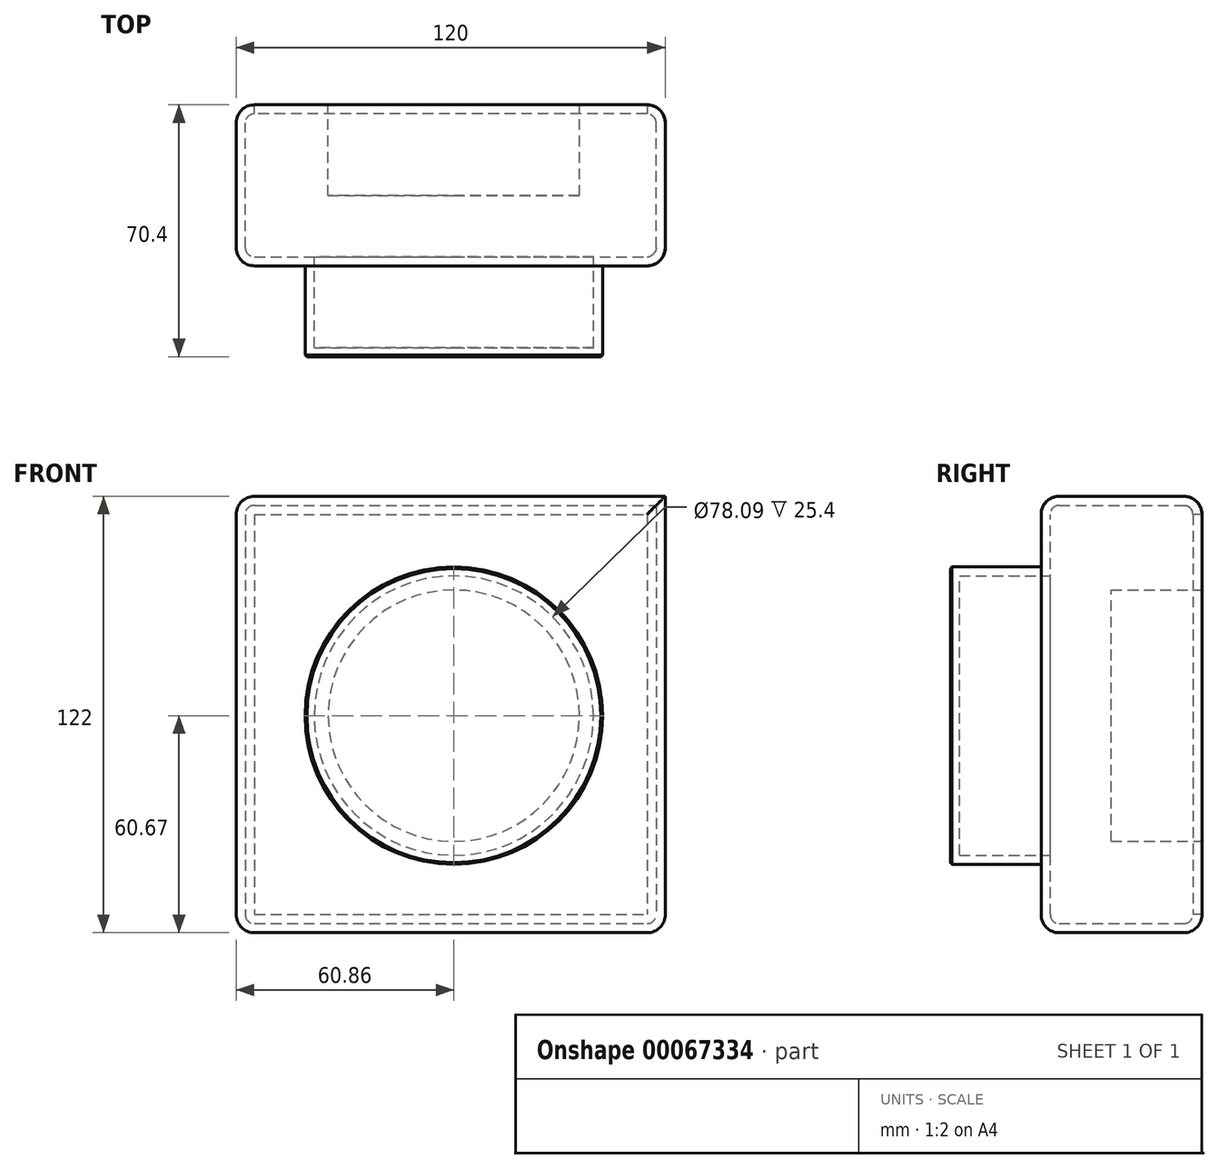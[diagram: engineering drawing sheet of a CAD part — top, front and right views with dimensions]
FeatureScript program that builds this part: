
annotation { "Feature Type Name" : "Feature", "Feature Type Description" : "" }
export const myFeature = defineFeature(function(context is Context, id is Id, definition is map)
    precondition{}
    {
        {
            var Q0;
            Q0=qCreatedBy(makeId("Front.planeOp"),FACE);
            var sketch = newSketch(context, id + "F0", { "sketchPlane" : qUnion([Q0])});
            skLineSegment(sketch, "E0.bottom", {"start": v(-60.86, 61.33) * mm, "end": v(59.14, 61.33) * mm});
            skLineSegment(sketch, "E0.top", {"start": v(-60.86, -60.67) * mm, "end": v(59.14, -60.67) * mm});
            skLineSegment(sketch, "E0.left", {"start": v(-60.86, 61.33) * mm, "end": v(-60.86, -60.67) * mm});
            skLineSegment(sketch, "E0.right", {"start": v(59.14, 61.33) * mm, "end": v(59.14, -60.67) * mm});
            skSolve(sketch);
        }
        {
            var Q0;
            Q0=makeQuery(id+"F0.imprint","IMPRINT",FACE,{"disambiguationData":[TD([[makeQuery(id+"F0.imprint","IMPRINT",EDGE,{"derivedFrom":sQuery(id+"F0.wireOp",EDGE,"E0.bottom")}),-1.0]])]});
            extrude(context, id + "F1", {"entities" : qUnion([Q0]), "depth" : 45 * mm});
        }
        {
            var Q0;
            Q0=makeQuery(id+"F1.opExtrude","CAP_FACE",FACE,{"disambiguationData":[OSD([sQuery(id+"F0.wireOp",EDGE,"E0.bottom"),sQuery(id+"F0.wireOp",EDGE,"E0.top"),sQuery(id+"F0.wireOp",EDGE,"E0.left"),sQuery(id+"F0.wireOp",EDGE,"E0.right")])],"isStart":false});
            var sketch = newSketch(context, id + "F2", { "sketchPlane" : qUnion([Q0])});
            skCircle(sketch, "E1", {"center": v(0, 0) * mm, "radius": 41.58 * mm});
            skSolve(sketch);
        }
        {
            var Q0;
            Q0=makeQuery(id+"F2.imprint","IMPRINT",FACE,{"disambiguationData":[TD([[makeQuery(id+"F2.imprint","IMPRINT",EDGE,{"derivedFrom":sQuery(id+"F2.wireOp",EDGE,"E1")}),1.0]])]});
            var sketch = newSketch(context, id + "F3", { "sketchPlane" : qUnion([Q0])});
            skCircle(sketch, "E2", {"center": v(0, 0) * mm, "radius": 35.37 * mm});
            skSolve(sketch);
        }
        {
            var Q0;
            Q0 = qSketchRegion(id + "F3", true);
            var Q1;
            Q1 = qSketchRegion(id + "F2", true);
            extrude(context, id + "F4", {"entities" : qUnion([Q0, Q1]), "operationType" : NewBodyOperationType.REMOVE, "depth" : 50.8 * mm});
        }
        {
            var Q0;
            Q0=makeQuery(id+"F1.opExtrude","SWEPT_EDGE",EDGE,{"disambiguationData":[OSD([sQuery(id+"F0.wireOp",EDGE,"E0.bottom"),sQuery(id+"F0.wireOp",EDGE,"E0.left")])]});
            var Q1;
            Q1=makeQuery(id+"F1.opExtrude","SWEPT_FACE",FACE,{"disambiguationData":[OSD([sQuery(id+"F0.wireOp",EDGE,"E0.left")])]});
            var Q2;
            Q2=makeQuery(id+"F1.opExtrude","CAP_EDGE",EDGE,{"disambiguationData":[OSD([sQuery(id+"F0.wireOp",EDGE,"E0.bottom")])],"isStart":false});
            var Q3;
            Q3=makeQuery(id+"F1.opExtrude","CAP_EDGE",EDGE,{"disambiguationData":[OSD([sQuery(id+"F0.wireOp",EDGE,"E0.bottom")])],"isStart":true});
            var Q4;
            Q4=makeQuery(id+"F1.opExtrude","CAP_EDGE",EDGE,{"disambiguationData":[OSD([sQuery(id+"F0.wireOp",EDGE,"E0.right")])],"isStart":true});
            var Q5;
            Q5=makeQuery(id+"F1.opExtrude","CAP_EDGE",EDGE,{"disambiguationData":[OSD([sQuery(id+"F0.wireOp",EDGE,"E0.right")])],"isStart":false});
            var Q6;
            Q6=makeQuery(id+"F1.opExtrude","SWEPT_EDGE",EDGE,{"disambiguationData":[OSD([sQuery(id+"F0.wireOp",EDGE,"E0.top"),sQuery(id+"F0.wireOp",EDGE,"E0.right")])]});
            var Q7;
            Q7=makeQuery(id+"F1.opExtrude","CAP_EDGE",EDGE,{"disambiguationData":[OSD([sQuery(id+"F0.wireOp",EDGE,"E0.top")])],"isStart":false});
            var Q8;
            Q8=makeQuery(id+"F1.opExtrude","CAP_EDGE",EDGE,{"disambiguationData":[OSD([sQuery(id+"F0.wireOp",EDGE,"E0.top")])],"isStart":true});
            fillet(context, id + "F5", {"entities" : qUnion([Q0, Q1, Q2, Q3, Q4, Q5, Q6, Q7, Q8]), "radius" : 5.08 * mm, "tangentPropagation" : true, "allowEdgeOverflow" : false});
        }
        {
            var Q0;
            Q0 = qSketchRegion(id + "F3", true);
            var Q1;
            Q1 = qSketchRegion(id + "F2", true);
            extrude(context, id + "F6", {"entities" : qUnion([Q0, Q1]), "operationType" : NewBodyOperationType.ADD, "depth" : 25.4 * mm});
        }
        {
            var Q0;
            Q0 = qSketchRegion(id + "F3", true);
            extrude(context, id + "F7", {"entities" : qUnion([Q0]), "operationType" : NewBodyOperationType.ADD, "oppositeDirection" : true, "depth" : 25.4 * mm});
        }
        {
            var Q0;
            Q0=sQuery(id+"F3.wireOp",EDGE,"E2");
            extrude(context, id + "F8", {"bodyType" : ToolBodyType.SURFACE, "surfaceEntities" : qUnion([Q0]), "depth" : 25.4 * mm});
        }
        {
            var Q0;
            Q0 = qSketchRegion(id + "F3", true);
            extrude(context, id + "F9", {"entities" : qUnion([Q0]), "operationType" : NewBodyOperationType.ADD, "oppositeDirection" : true, "depth" : 25.4 * mm});
        }
        {
            var Q0;
            Q0=makeQuery(id+"F6.opExtrude","CAP_EDGE",EDGE,{"disambiguationData":[OSD([sQuery(id+"F2.wireOp",EDGE,"E1")])],"isStart":false});
            chamfer(context, id + "F10", {"entities" : qUnion([Q0]), "width" : .5 * mm, "tangentPropagation" : true});
        }
        {
            var Q0;
            Q0=makeQuery(id+"F1.opExtrude","CAP_FACE",FACE,{"disambiguationData":[OSD([sQuery(id+"F0.wireOp",EDGE,"E0.bottom"),sQuery(id+"F0.wireOp",EDGE,"E0.top"),sQuery(id+"F0.wireOp",EDGE,"E0.left"),sQuery(id+"F0.wireOp",EDGE,"E0.right")])],"isStart":true});
            shell(context, id + "F11", {"entities" : qUnion([Q0]), "thickness" : 2.54 * mm});
        }
        {
            var Q0;
            Q0=qCreatedBy(makeId("Front.planeOp"),FACE);
            var sketch = newSketch(context, id + "F12", { "sketchPlane" : qUnion([Q0])});
            skCircle(sketch, "E3", {"center": v(0, 0) * mm, "radius": 35.14 * mm});
            skSolve(sketch);
        }
        {
            var Q0;
            Q0 = qSketchRegion(id + "F12", true);
            extrude(context, id + "F13", {"entities" : qUnion([Q0]), "depth" : 25.4 * mm});
        }
    });
